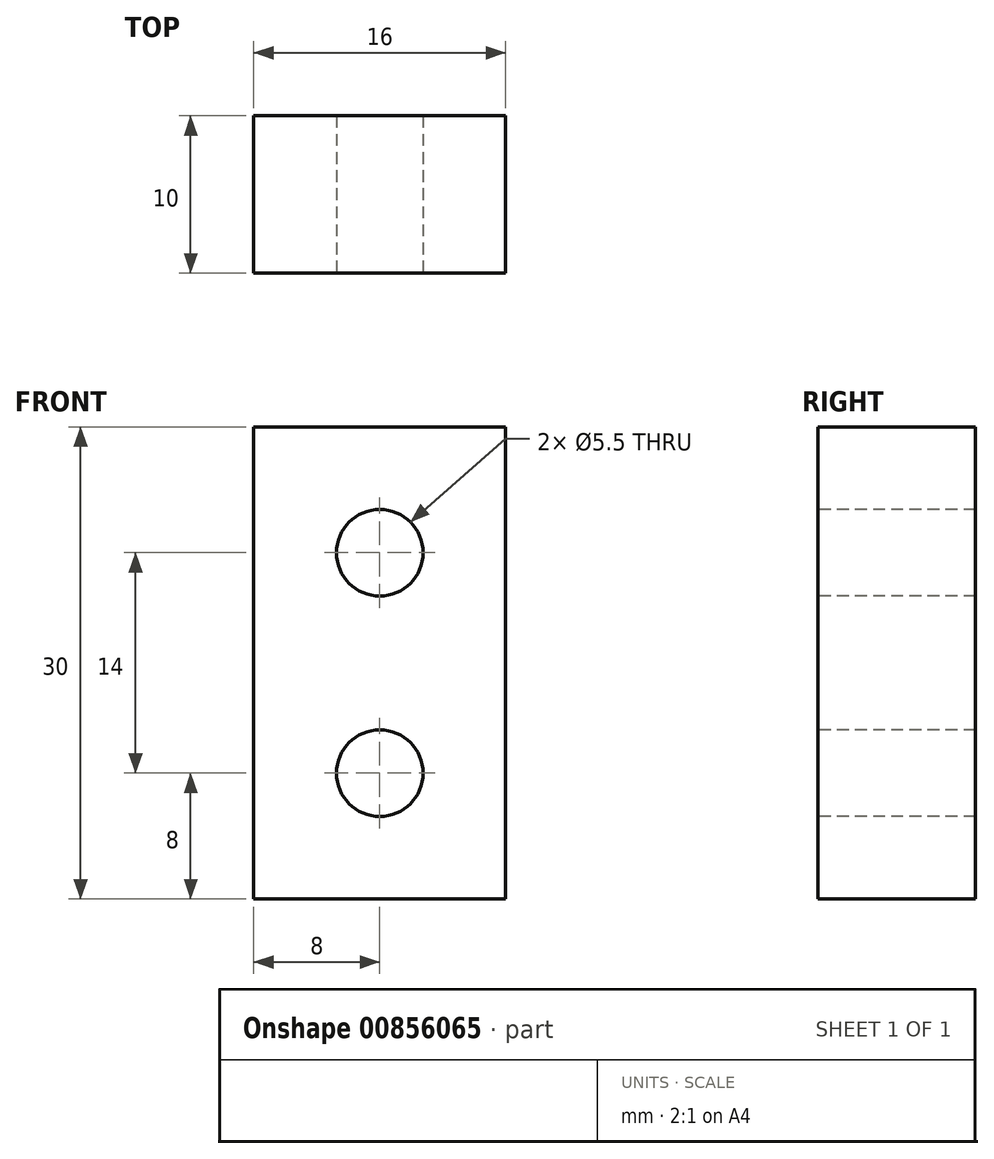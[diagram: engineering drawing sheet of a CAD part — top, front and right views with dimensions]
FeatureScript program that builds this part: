
annotation { "Feature Type Name" : "Feature", "Feature Type Description" : "" }
export const myFeature = defineFeature(function(context is Context, id is Id, definition is map)
    precondition{}
    {
        {
            var Q0;
            Q0=qCreatedBy(makeId("Front.planeOp"),FACE);
            var sketch = newSketch(context, id + "F0", { "sketchPlane" : qUnion([Q0])});
            skLineSegment(sketch, "E0.bottom", {"start": v(8, 15) * mm, "end": v(-8, 15) * mm});
            skLineSegment(sketch, "E0.top", {"start": v(8, -15) * mm, "end": v(-8, -15) * mm});
            skLineSegment(sketch, "E0.left", {"start": v(8, 15) * mm, "end": v(8, -15) * mm});
            skLineSegment(sketch, "E0.right", {"start": v(-8, 15) * mm, "end": v(-8, -15) * mm});
            skPoint(sketch, "E0.middle", {"position": v(0, 0) * mm});
            skSolve(sketch);
        }
        {
            var Q0;
            Q0=makeQuery(id+"F0.imprint","IMPRINT",FACE,{"disambiguationData":[TD([[makeQuery(id+"F0.imprint","IMPRINT",EDGE,{"derivedFrom":sQuery(id+"F0.wireOp",EDGE,"E0.bottom")}),1.0]])]});
            extrude(context, id + "F1", {"entities" : qUnion([Q0]), "depth" : 10 * mm, "offsetDistance" : 25 * mm});
        }
        {
            var Q0;
            Q0=makeQuery(id+"F1.opExtrude","CAP_FACE",FACE,{"disambiguationData":[OSD([sQuery(id+"F0.wireOp",EDGE,"E0.bottom"),sQuery(id+"F0.wireOp",EDGE,"E0.top"),sQuery(id+"F0.wireOp",EDGE,"E0.left"),sQuery(id+"F0.wireOp",EDGE,"E0.right")])],"isStart":false});
            var sketch = newSketch(context, id + "F2", { "sketchPlane" : qUnion([Q0])});
            skLineSegment(sketch, "E1", {"start": v(0, 15) * mm, "end": v(0, 7) * mm});
            skLineSegment(sketch, "E2", {"start": v(0, -15) * mm, "end": v(0, -7) * mm});
            skSolve(sketch);
        }
        {
            var Q0;
            Q0=sQuery(id+"F2.wireOp",VERTEX,"E1.end");
            var Q1;
            Q1=sQuery(id+"F2.wireOp",VERTEX,"E2.end");
            var Q2;
            Q2=makeQuery(id+"F1.opExtrude","SWEPT_BODY",BODY,{"disambiguationData":[OSD([sQuery(id+"F0.wireOp",EDGE,"E0.bottom"),sQuery(id+"F0.wireOp",EDGE,"E0.top"),sQuery(id+"F0.wireOp",EDGE,"E0.left"),sQuery(id+"F0.wireOp",EDGE,"E0.right")])]});
            hole(context, id + "F3", {"style" : HoleStyle.SIMPLE, "endStyle" : HoleEndStyle.THROUGH, "standardTappedOrClearance" : lookupTablePath({ "fit" : "Normal", "standard" : "ISO", "size" : "M5", "type" : "Clearance" }), "standardBlindInLast" : lookupTablePath({ "fit" : "Standard", "standard" : "ISO", "size" : "M5", "type" : "Clearance" }), "holeDiameter" : 5.5 * mm, "majorDiameter" : 5 * mm, "isTappedThrough" : true, "tappedDepth" : 12 * mm, "tapClearance" : 3, "locations" : qUnion([Q0, Q1]), "scope" : qUnion([Q2])});
        }
    });
